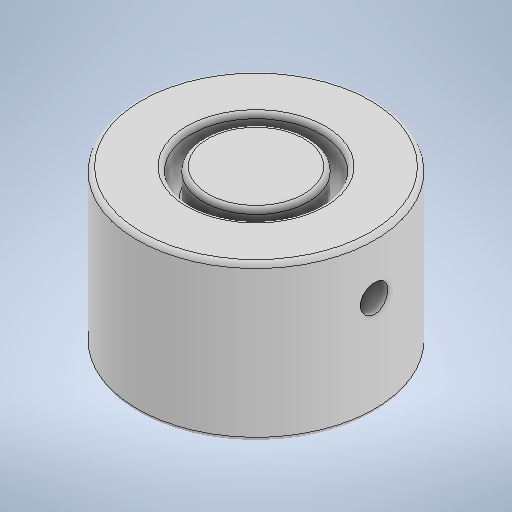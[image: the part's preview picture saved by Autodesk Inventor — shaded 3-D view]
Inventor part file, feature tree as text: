
AUTODESK INVENTOR PART (.ipt)
format: ipt  version: 2025.1 (Build 291241000, 241)  size: 272,896 bytes
history: native  units: mm
features: extrude x3, sketch x3, fillet x1
ambient origin geometry x8: Origin, YZ Plane, XZ Plane, XY Plane, X Axis, Y Axis, Z Axis, Center Point
bodies: Solide1 (feature_tree)
feature tree (7):
  extrude  "Extrusion1"  Depth=26.0mm
  extrude  "Extrusion2"  Depth=17.0mm TaperAngle=0.0deg
  fillet  "Congé1"  Radius=11.5mm
  extrude  "Extrusion3"  Depth=14.2mm
  sketch  "Esquisse1"
  sketch  "Esquisse2"
  sketch  "Esquisse3"
